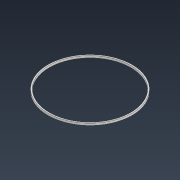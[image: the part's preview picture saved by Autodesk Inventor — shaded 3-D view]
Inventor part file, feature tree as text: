
AUTODESK INVENTOR PART (.ipt)
format: ipt  version: 2022 (Build 260153000, 153)  size: 83,456 bytes
history: native  units: mm
features: extrude x1, sketch x1
ambient origin geometry x8: Origin, YZ Plane, XZ Plane, XY Plane, X Axis, Y Axis, Z Axis, Center Point
bodies: Solid1 (feature_tree)
feature tree (2):
  extrude  "Extrusion1"  Depth=2.0mm
  sketch  "Sketch1"  dims[d0=83.0mm d1=85.5mm d2=2.0mm d3=0.0mm]
